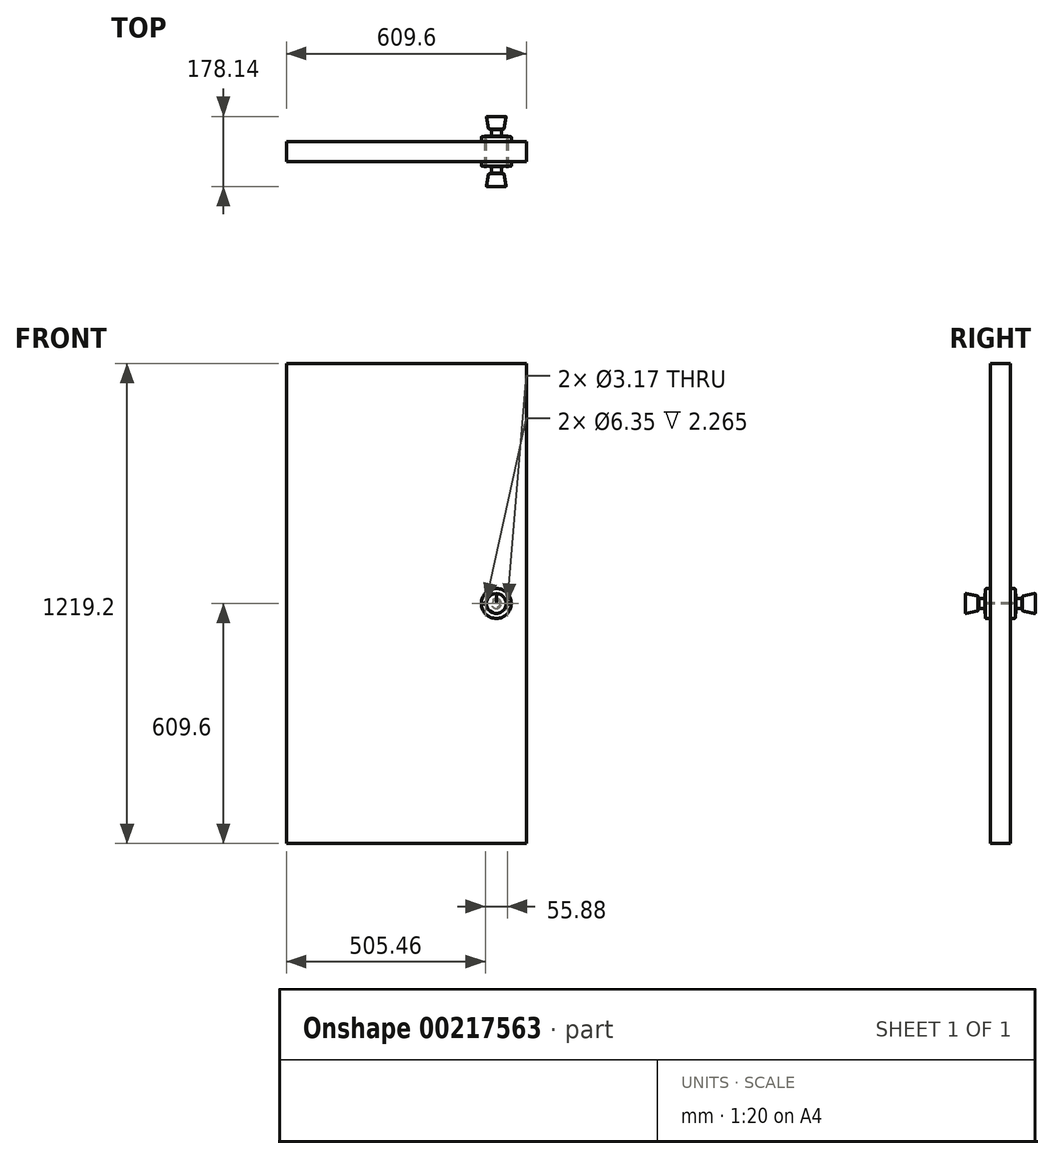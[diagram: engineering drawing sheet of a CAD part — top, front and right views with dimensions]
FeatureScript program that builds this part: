
annotation { "Feature Type Name" : "Feature", "Feature Type Description" : "" }
export const myFeature = defineFeature(function(context is Context, id is Id, definition is map)
    precondition{}
    {
        {
            var Q0;
            Q0=qCreatedBy(makeId("Front.planeOp"),FACE);
            var sketch = newSketch(context, id + "F0", { "sketchPlane" : qUnion([Q0])});
            skLineSegment(sketch, "E0.bottom", {"start": v(304.8, 609.6) * mm, "end": v(-304.8, 609.6) * mm});
            skLineSegment(sketch, "E0.top", {"start": v(304.8, -609.6) * mm, "end": v(-304.8, -609.6) * mm});
            skLineSegment(sketch, "E0.left", {"start": v(304.8, 609.6) * mm, "end": v(304.8, -609.6) * mm});
            skLineSegment(sketch, "E0.right", {"start": v(-304.8, 609.6) * mm, "end": v(-304.8, -609.6) * mm});
            skPoint(sketch, "E0.middle", {"position": v(0, 0) * mm});
            skPoint(sketch, "E1", {"position": v(228.6, 0) * mm});
            skPoint(sketch, "E1.positionSnap0", {"position": v(304.8, 0) * mm});
            skSolve(sketch);
        }
        {
            var Q0;
            Q0 = qSketchRegion(id + "F0", true);
            extrude(context, id + "F1", {"entities" : qUnion([Q0]), "endBound" : BoundingType.SYMMETRIC, "depth" : 50.8 * mm});
        }
        {
            var Q0;
            Q0=qCreatedBy(makeId("Right.planeOp"),FACE);
            var Q1;
            Q1=sQuery(id+"F0.wireOp",VERTEX,"E1");
            cPlane(context, id + "F2", {"entities" : qUnion([Q0, Q1]), "cplaneType" : CPlaneType.PLANE_POINT, "offset" : 25.4 * mm, "width" : 152.4 * mm, "height" : 152.4 * mm});
        }
        {
            var Q0;
            Q0=qCreatedBy(id+"F2.planeOp",FACE);
            var sketch = newSketch(context, id + "F3", { "sketchPlane" : qUnion([Q0])});
            skLineSegment(sketch, "E2.bottom", {"start": v(-25.4, 38.1) * mm, "end": v(-38.1, 38.1) * mm});
            skLineSegment(sketch, "E2.top", {"start": v(-25.4, 0) * mm, "end": v(-38.1, 0) * mm});
            skLineSegment(sketch, "E2.left", {"start": v(-25.4, 38.1) * mm, "end": v(-25.4, 0) * mm});
            skPoint(sketch, "E3", {"position": v(-25.4, 19.05) * mm});
            skFitSpline(sketch, "E4", {"points": [v(-38.1, 38.1) * mm, v(-38.1, 0) * mm], "startDerivative": vector(5.77, -11) * mm, "endDerivative": vector(9.06, -85.76) * mm});
            skLineSegment(sketch, "E5", {"start": v(-39.02, 12.7) * mm, "end": v(-54.9, 12.7) * mm});
            skLineSegment(sketch, "E6", {"start": v(-54.9, 12.7) * mm, "end": v(-54.9, 0) * mm});
            skLineSegment(sketch, "E7", {"start": v(-54.9, 9.53) * mm, "end": v(-56.49, 9.53) * mm});
            skLineSegment(sketch, "E8", {"start": v(-56.49, 9.53) * mm, "end": v(-56.49, 0) * mm});
            skLineSegment(sketch, "E9", {"start": v(-56.49, 9.53) * mm, "end": v(-56.49, 19.05) * mm});
            skLineSegment(sketch, "E10", {"start": v(-56.49, 19.05) * mm, "end": v(-88.24, 25.4) * mm});
            skFitSpline(sketch, "E11", {"points": [v(-88.24, 25.4) * mm, v(-88.24, 0) * mm], "startDerivative": vector(-7.66, -12.98) * mm, "endDerivative": vector(-5.15, -63.54) * mm});
            skLineSegment(sketch, "E12", {"start": v(-88.24, 0) * mm, "end": v(-38.1, 0) * mm});
            skLineSegment(sketch, "E13.MirrorCS", {"start": v(54.9, 9.53) * mm, "end": v(56.49, 9.53) * mm});
            skLineSegment(sketch, "E14.MirrorCS", {"start": v(56.49, 9.53) * mm, "end": v(56.49, 19.05) * mm});
            skLineSegment(sketch, "E15.MirrorCS", {"start": v(25.4, 0) * mm, "end": v(38.1, 0) * mm});
            skFitSpline(sketch, "E16.MirrorCS", {"points": [v(38.1, 38.1) * mm, v(38.1, 0) * mm], "startDerivative": vector(-5.77, -11) * mm, "endDerivative": vector(-9.06, -85.76) * mm});
            skLineSegment(sketch, "E17.MirrorCS", {"start": v(88.24, 0) * mm, "end": v(38.1, 0) * mm});
            skFitSpline(sketch, "E18.MirrorCS", {"points": [v(88.24, 25.4) * mm, v(88.24, 0) * mm], "startDerivative": vector(7.66, -12.98) * mm, "endDerivative": vector(5.15, -63.54) * mm});
            skLineSegment(sketch, "E19.MirrorCS", {"start": v(25.4, 38.1) * mm, "end": v(38.1, 38.1) * mm});
            skLineSegment(sketch, "E20.MirrorCS", {"start": v(56.49, 19.05) * mm, "end": v(88.24, 25.4) * mm});
            skLineSegment(sketch, "E21.MirrorCS", {"start": v(39.02, 12.7) * mm, "end": v(54.9, 12.7) * mm});
            skLineSegment(sketch, "E22.MirrorCS", {"start": v(25.4, 38.1) * mm, "end": v(25.4, 0) * mm});
            skLineSegment(sketch, "E23.MirrorCS", {"start": v(56.49, 9.53) * mm, "end": v(56.49, 0) * mm});
            skLineSegment(sketch, "E24.MirrorCS", {"start": v(54.9, 12.7) * mm, "end": v(54.9, 0) * mm});
            skSolve(sketch);
        }
        {
            var Q0;
            Q0 = qSketchRegion(id + "F3", true);
            var Q1;
            Q1=sQuery(id+"F3.wireOp",EDGE,"E2.top");
            revolve(context, id + "F4", {"operationType" : NewBodyOperationType.ADD, "entities" : qUnion([Q0]), "axis" : qUnion([Q1]), "revolveType" : RevolveType.FULL});
        }
        {
            var Q0;
            Q0=makeQuery(id+"F4.opRevolve","SWEPT_EDGE",EDGE,{"disambiguationData":[OSD([sQuery(id+"F3.wireOp",EDGE,"E10"),sQuery(id+"F3.wireOp",EDGE,"E11")])]});
            var Q1;
            Q1=makeQuery(id+"F4.opRevolve","SWEPT_EDGE",EDGE,{"disambiguationData":[OSD([sQuery(id+"F3.wireOp",EDGE,"E9"),sQuery(id+"F3.wireOp",EDGE,"E10")])]});
            var Q2;
            Q2=makeQuery(id+"F4.opRevolve","SWEPT_EDGE",EDGE,{"disambiguationData":[OSD([sQuery(id+"F3.wireOp",EDGE,"E4"),sQuery(id+"F3.wireOp",EDGE,"E5")])]});
            var Q3;
            Q3=makeQuery(id+"F4.opRevolve","SWEPT_EDGE",EDGE,{"disambiguationData":[OSD([sQuery(id+"F3.wireOp",EDGE,"E14.MirrorCS"),sQuery(id+"F3.wireOp",EDGE,"E20.MirrorCS")])]});
            var Q4;
            Q4=makeQuery(id+"F4.opRevolve","SWEPT_EDGE",EDGE,{"disambiguationData":[OSD([sQuery(id+"F3.wireOp",EDGE,"E18.MirrorCS"),sQuery(id+"F3.wireOp",EDGE,"E20.MirrorCS")])]});
            var Q5;
            Q5=makeQuery(id+"F4.opRevolve","SWEPT_EDGE",EDGE,{"disambiguationData":[OSD([sQuery(id+"F3.wireOp",EDGE,"E16.MirrorCS"),sQuery(id+"F3.wireOp",EDGE,"E21.MirrorCS")])]});
            var Q6;
            Q6=makeQuery(id+"F4.opRevolve","SWEPT_EDGE",EDGE,{"disambiguationData":[OSD([sQuery(id+"F3.wireOp",EDGE,"E2.bottom"),sQuery(id+"F3.wireOp",EDGE,"E4")])]});
            var Q7;
            Q7=makeQuery(id+"F4.opRevolve","SWEPT_EDGE",EDGE,{"disambiguationData":[OSD([sQuery(id+"F3.wireOp",EDGE,"E16.MirrorCS"),sQuery(id+"F3.wireOp",EDGE,"E19.MirrorCS")])]});
            fillet(context, id + "F5", {"entities" : qUnion([Q0, Q1, Q2, Q3, Q4, Q5, Q6, Q7]), "radius" : 1.59 * mm, "tangentPropagation" : true, "allowEdgeOverflow" : false});
        }
        {
            var Q0;
            Q0=sQuery(id+"F3.wireOp",EDGE,"E4");
            cPoint(context, id + "F6", {"entities" : qUnion([Q0]), "parameter" : 0.5});
        }
        {
            var Q0;
            Q0=qCreatedBy(makeId("Front.planeOp"),FACE);
            var Q1;
            Q1 = qCreatedBy(id + "F6" ,VERTEX);
            cPlane(context, id + "F7", {"entities" : qUnion([Q0, Q1]), "cplaneType" : CPlaneType.PLANE_POINT, "offset" : 25.4 * mm, "width" : 152.4 * mm, "height" : 152.4 * mm});
        }
        {
            var Q0;
            Q0=qCreatedBy(id+"F7.planeOp",FACE);
            var sketch = newSketch(context, id + "F8", { "sketchPlane" : qUnion([Q0])});
            skCircle(sketch, "E25", {"center": v(256.54, 0) * mm, "radius": 3.18 * mm});
            skLineSegment(sketch, "E26", {"start": v(228.6, -15.12) * mm, "end": v(228.6, 48.27) * mm});
            skCircle(sketch, "E27.MirrorC", {"center": v(200.66, 0) * mm, "radius": 3.18 * mm});
            skSolve(sketch);
        }
        {
            var Q0;
            Q0=sQuery(id+"F8.wireOp",VERTEX,"E25.center");
            var Q1;
            Q1=sQuery(id+"F8.wireOp",VERTEX,"E27.MirrorC.center");
            var Q2;
            Q2=makeQuery(id+"F1.opExtrude","SWEPT_BODY",BODY,{"disambiguationData":[OSD([sQuery(id+"F0.wireOp",EDGE,"E0.bottom"),sQuery(id+"F0.wireOp",EDGE,"E0.top"),sQuery(id+"F0.wireOp",EDGE,"E0.left"),sQuery(id+"F0.wireOp",EDGE,"E0.right")])]});
            hole(context, id + "F9", {"style" : HoleStyle.C_BORE, "endStyle" : HoleEndStyle.BLIND, "holeDiameter" : 3.17 * mm, "cBoreDiameter" : 6.35 * mm, "cBoreDepth" : 1.59 * mm, "holeDepth" : 69.85 * mm, "locations" : qUnion([Q0, Q1]), "scope" : qUnion([Q2])});
        }
    });
